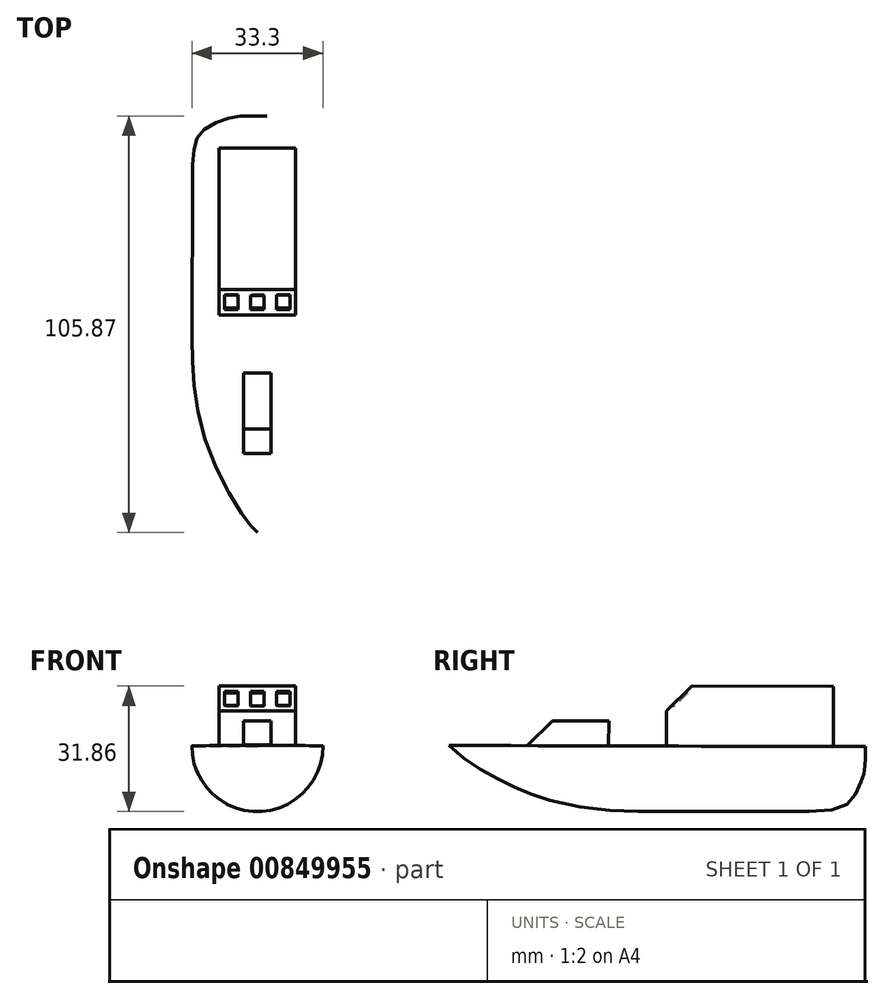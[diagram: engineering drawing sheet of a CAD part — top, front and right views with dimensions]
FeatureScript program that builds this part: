
annotation { "Feature Type Name" : "Feature", "Feature Type Description" : "" }
export const myFeature = defineFeature(function(context is Context, id is Id, definition is map)
    precondition{}
    {
        {
            var Q0;
            Q0=qCreatedBy(makeId("Right.planeOp"),FACE);
            var sketch = newSketch(context, id + "F0", { "sketchPlane" : qUnion([Q0])});
            skFitSpline(sketch, "E0", {"points": [v(-70.87, 10.93) * mm, v(-68.1, 8.37) * mm, v(-47.17, -2.46) * mm, v(-23.81, -5.82) * mm, v(-7.18, -5.82) * mm, v(19.7, -5.82) * mm, v(28.23, -5.1) * mm, v(31.72, -2.57) * mm, v(34.48, 3.59) * mm, v(34.92, 10.6) * mm], "startDerivative": vector(35, -32.2) * mm, "endDerivative": vector(-5.03, 129.97) * mm});
            skLineSegment(sketch, "E1", {"start": v(34.92, 10.6) * mm, "end": v(-70.87, 10.93) * mm});
            skSolve(sketch);
        }
        {
            var Q0;
            Q0 = qSketchRegion(id + "F0", true);
            var Q1;
            Q1=sQuery(id+"F0.wireOp",EDGE,"E0");
            var Q2;
            Q2=sQuery(id+"F0.wireOp",EDGE,"E1");
            revolve(context, id + "F1", {"surfaceOperationType" : NewSurfaceOperationType.NEW, "entities" : qUnion([Q0]), "surfaceEntities" : qUnion([Q1]), "axis" : qUnion([Q2]), "revolveType" : RevolveType.TWO_DIRECTIONS, "angle" : 90 * degree, "angleBack" : 270 * degree});
        }
        {
            var Q0;
            Q0=makeQuery(id+"F1.opRevolve","CAP_FACE",FACE,{"disambiguationData":[OSD([sQuery(id+"F0.wireOp",EDGE,"E0"),sQuery(id+"F0.wireOp",EDGE,"E1")])],"isStart":false});
            var sketch = newSketch(context, id + "F2", { "sketchPlane" : qUnion([Q0])});
            skLineSegment(sketch, "E2.bottom", {"start": v(9.75, 26.74) * mm, "end": v(-9.75, 26.74) * mm});
            skLineSegment(sketch, "E2.top", {"start": v(9.75, -15.6) * mm, "end": v(-9.75, -15.6) * mm});
            skLineSegment(sketch, "E2.left", {"start": v(9.75, 26.74) * mm, "end": v(9.75, -15.6) * mm});
            skLineSegment(sketch, "E2.right", {"start": v(-9.75, 26.74) * mm, "end": v(-9.75, -15.6) * mm});
            skPoint(sketch, "E2.middle", {"position": v(0, 5.58) * mm});
            skLineSegment(sketch, "E3.bottom", {"start": v(-3.46, -30.3) * mm, "end": v(3.46, -30.3) * mm});
            skLineSegment(sketch, "E3.top", {"start": v(-3.46, -50.82) * mm, "end": v(3.46, -50.82) * mm});
            skLineSegment(sketch, "E3.left", {"start": v(-3.46, -30.3) * mm, "end": v(-3.46, -50.82) * mm});
            skLineSegment(sketch, "E3.right", {"start": v(3.46, -30.3) * mm, "end": v(3.46, -50.82) * mm});
            skPoint(sketch, "E3.middle", {"position": v(0, -40.56) * mm});
            skSolve(sketch);
        }
        {
            var Q0;
            Q0=makeQuery(id+"F2.imprint","IMPRINT",FACE,{"disambiguationData":[TD([[makeQuery(id+"F2.imprint","IMPRINT",EDGE,{"derivedFrom":sQuery(id+"F2.wireOp",EDGE,"E2.bottom")}),1.0]])]});
            extrude(context, id + "F3", {"entities" : qUnion([Q0]), "operationType" : NewBodyOperationType.ADD, "depth" : 15.24 * mm, "offsetDistance" : 25.4 * mm});
        }
        {
            var Q0;
            Q0=makeQuery(id+"F2.imprint","IMPRINT",FACE,{"disambiguationData":[TD([[makeQuery(id+"F2.imprint","IMPRINT",EDGE,{"derivedFrom":sQuery(id+"F2.wireOp",EDGE,"E3.bottom")}),-1.0]])]});
            extrude(context, id + "F4", {"entities" : qUnion([Q0]), "operationType" : NewBodyOperationType.ADD, "depth" : 6.35 * mm, "offsetDistance" : 25.4 * mm});
        }
        {
            var Q0;
            Q0=makeQuery(id+"F3.opExtrude","CAP_EDGE",EDGE,{"disambiguationData":[OSD([sQuery(id+"F2.wireOp",EDGE,"E2.top")])],"isStart":false});
            chamfer(context, id + "F5", {"entities" : qUnion([Q0]), "width" : 6.35 * mm, "tangentPropagation" : true});
        }
        {
            var Q0;
            Q0=makeQuery(id+"F4.opExtrude","CAP_EDGE",EDGE,{"disambiguationData":[OSD([sQuery(id+"F2.wireOp",EDGE,"E3.top")])],"isStart":false});
            chamfer(context, id + "F6", {"entities" : qUnion([Q0]), "width" : 6.22 * mm, "tangentPropagation" : true});
        }
        {
            var Q0;
            Q0=makeQuery(id+"F5.opChamfer","BLEND_FACE",FACE,{"disambiguationData":[OSD([sQuery(id+"F2.wireOp",EDGE,"E2.top")])]});
            var sketch = newSketch(context, id + "F7", { "sketchPlane" : qUnion([Q0])});
            skLineSegment(sketch, "E4.bottom", {"start": v(1.71, 9.84) * mm, "end": v(-1.71, 9.84) * mm});
            skLineSegment(sketch, "E4.top", {"start": v(1.71, 4.76) * mm, "end": v(-1.71, 4.76) * mm});
            skLineSegment(sketch, "E4.left", {"start": v(1.71, 9.84) * mm, "end": v(1.71, 4.76) * mm});
            skLineSegment(sketch, "E4.right", {"start": v(-1.71, 9.84) * mm, "end": v(-1.71, 4.76) * mm});
            skPoint(sketch, "E4.middle", {"position": v(0, 7.3) * mm});
            skLineSegment(sketch, "E5.bottom", {"start": v(8.32, 9.87) * mm, "end": v(4.89, 9.87) * mm});
            skLineSegment(sketch, "E5.top", {"start": v(8.32, 4.79) * mm, "end": v(4.89, 4.79) * mm});
            skLineSegment(sketch, "E5.left", {"start": v(8.32, 9.87) * mm, "end": v(8.32, 4.79) * mm});
            skLineSegment(sketch, "E5.right", {"start": v(4.89, 9.87) * mm, "end": v(4.89, 4.79) * mm});
            skPoint(sketch, "E5.middle", {"position": v(6.6, 7.33) * mm});
            skPoint(sketch, "E5.middle.positionSnap0", {"position": v(9.75, 7.33) * mm});
            skPoint(sketch, "E5.centerSnap0", {"position": v(9.75, 7.33) * mm});
            skLineSegment(sketch, "E6.bottom", {"start": v(-4.89, 9.87) * mm, "end": v(-8.32, 9.87) * mm});
            skLineSegment(sketch, "E6.top", {"start": v(-4.89, 4.79) * mm, "end": v(-8.32, 4.79) * mm});
            skLineSegment(sketch, "E6.left", {"start": v(-4.89, 9.87) * mm, "end": v(-4.89, 4.79) * mm});
            skLineSegment(sketch, "E6.right", {"start": v(-8.32, 9.87) * mm, "end": v(-8.32, 4.79) * mm});
            skPoint(sketch, "E6.middle", {"position": v(-6.6, 7.33) * mm});
            skPoint(sketch, "E6.middle.positionSnap0", {"position": v(-9.75, 7.33) * mm});
            skPoint(sketch, "E6.centerSnap0", {"position": v(-9.75, 7.33) * mm});
            skSolve(sketch);
        }
        {
            var Q0;
            Q0 = qSketchRegion(id + "F7", true);
            extrude(context, id + "F8", {"entities" : qUnion([Q0]), "operationType" : NewBodyOperationType.REMOVE, "oppositeDirection" : true, "depth" : 0.5 * mm, "offsetDistance" : 25.4 * mm});
        }
    });
